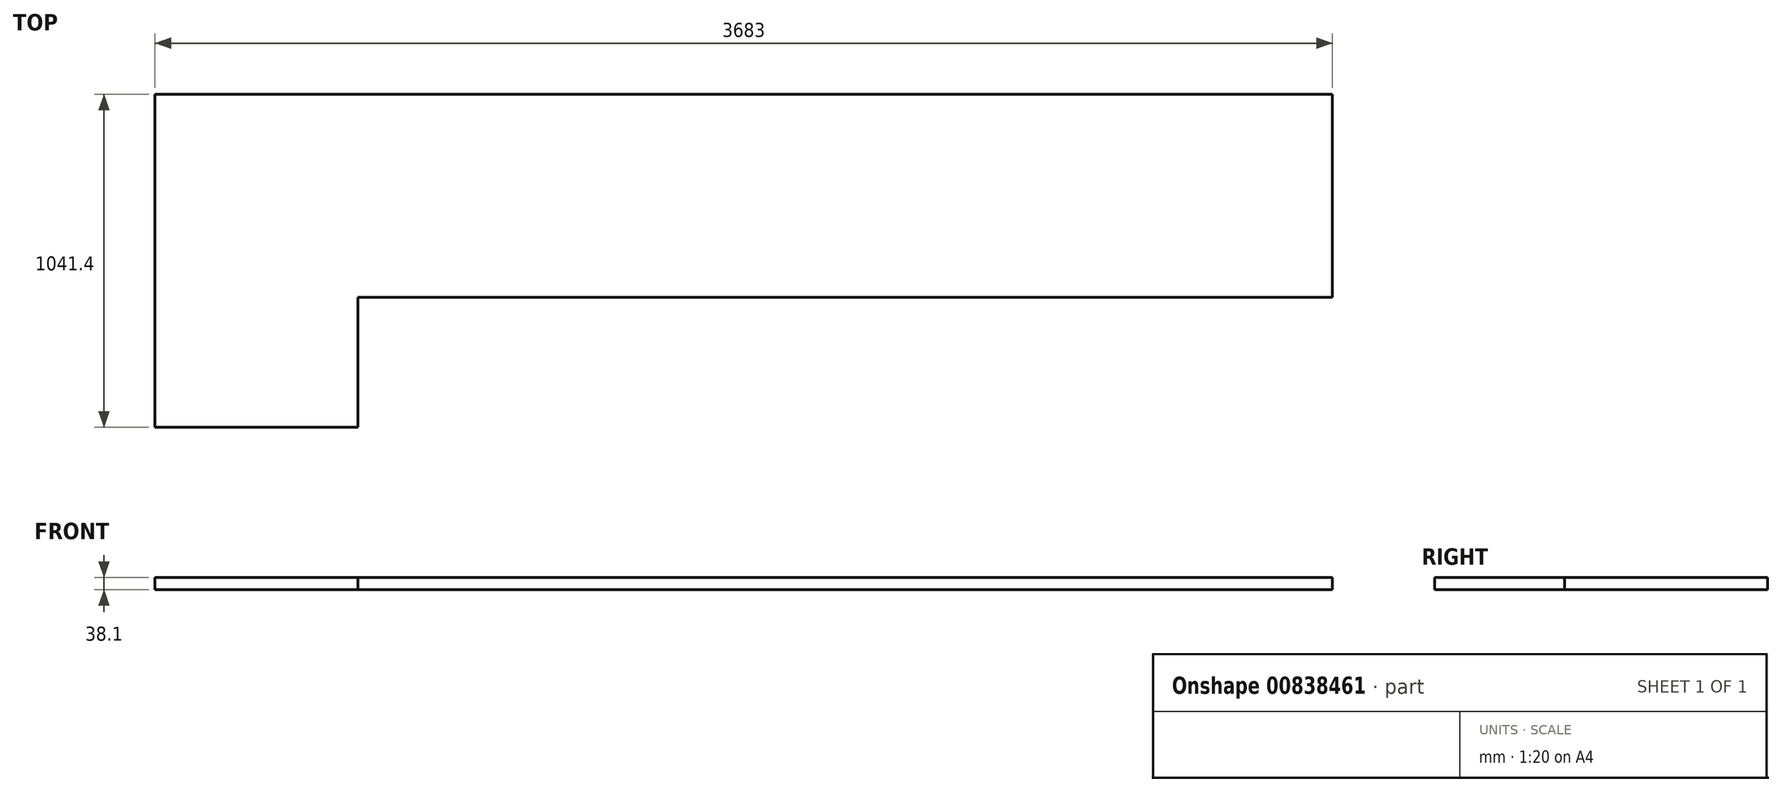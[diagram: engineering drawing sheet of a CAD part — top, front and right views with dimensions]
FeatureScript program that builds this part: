
annotation { "Feature Type Name" : "Feature", "Feature Type Description" : "" }
export const myFeature = defineFeature(function(context is Context, id is Id, definition is map)
    precondition{}
    {
        {
            var Q0;
            Q0=qCreatedBy(makeId("Top.planeOp"),FACE);
            var sketch = newSketch(context, id + "F0", { "sketchPlane" : qUnion([Q0])});
            skLineSegment(sketch, "E0", {"start": v(-635, -406.4) * mm, "end": v(-635, 635) * mm});
            skLineSegment(sketch, "E1", {"start": v(-635, 635) * mm, "end": v(3048, 635) * mm});
            skLineSegment(sketch, "E2", {"start": v(3048, 635) * mm, "end": v(3048, 0) * mm});
            skLineSegment(sketch, "E3", {"start": v(3048, 0) * mm, "end": v(0, 0) * mm});
            skLineSegment(sketch, "E4", {"start": v(0, 0) * mm, "end": v(0, -406.4) * mm});
            skLineSegment(sketch, "E5", {"start": v(0, -406.4) * mm, "end": v(-635, -406.4) * mm});
            skSolve(sketch);
        }
        {
            var Q0;
            Q0 = qSketchRegion(id + "F0", true);
            extrude(context, id + "F1", {"entities" : qUnion([Q0]), "depth" : 38.1 * mm, "offsetDistance" : 25.4 * mm});
        }
    });
